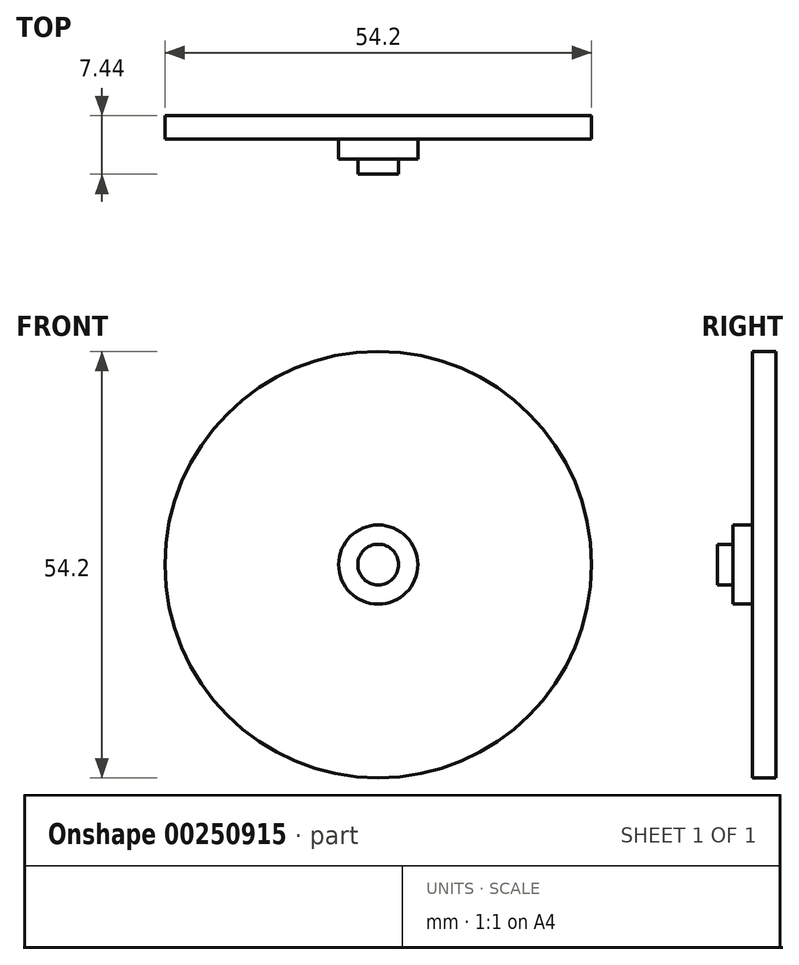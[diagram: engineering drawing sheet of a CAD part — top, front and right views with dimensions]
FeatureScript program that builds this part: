
annotation { "Feature Type Name" : "Feature", "Feature Type Description" : "" }
export const myFeature = defineFeature(function(context is Context, id is Id, definition is map)
    precondition{}
    {
        {
            var Q0;
            Q0=qCreatedBy(makeId("Front.planeOp"),FACE);
            var sketch = newSketch(context, id + "F0", { "sketchPlane" : qUnion([Q0])});
            skCircle(sketch, "E0", {"center": v(0, 0) * mm, "radius": 27.1 * mm});
            skSolve(sketch);
        }
        {
            var Q0;
            Q0=makeQuery(id+"F0.imprint","IMPRINT",FACE,{"disambiguationData":[TD([[makeQuery(id+"F0.imprint","IMPRINT",EDGE,{"derivedFrom":sQuery(id+"F0.wireOp",EDGE,"E0")}),1.0]])]});
            extrude(context, id + "F1", {"entities" : qUnion([Q0]), "endBound" : BoundingType.SYMMETRIC, "depth" : 3 * mm});
        }
        {
            var Q0;
            Q0=makeQuery(id+"F1.opExtrude","CAP_FACE",FACE,{"disambiguationData":[OSD([sQuery(id+"F0.wireOp",EDGE,"E0")])],"isStart":false});
            var sketch = newSketch(context, id + "F2", { "sketchPlane" : qUnion([Q0])});
            skCircle(sketch, "E1", {"center": v(0, 0) * mm, "radius": 5.03 * mm});
            skSolve(sketch);
        }
        {
            var Q0;
            Q0=makeQuery(id+"F2.imprint","IMPRINT",FACE,{"disambiguationData":[TD([[makeQuery(id+"F2.imprint","IMPRINT",EDGE,{"derivedFrom":sQuery(id+"F2.wireOp",EDGE,"E1")}),1.0]])]});
            extrude(context, id + "F3", {"entities" : qUnion([Q0]), "operationType" : NewBodyOperationType.ADD, "depth" : 2.5 * mm});
        }
        {
            var Q0;
            Q0=makeQuery(id+"F3.opExtrude","CAP_FACE",FACE,{"disambiguationData":[OSD([sQuery(id+"F2.wireOp",EDGE,"E1")])],"isStart":false});
            shell(context, id + "F4", {"entities" : qUnion([Q0]), "thickness" : 2.44 * mm});
        }
        {
            var Q0;
            Q0=makeQuery(id+"F4.opShell","OFFSET_FACE",FACE,{"disambiguationData":[OSD([sQuery(id+"F0.wireOp",EDGE,"E0")])]});
            extrude(context, id + "F5", {"entities" : qUnion([Q0]), "operationType" : NewBodyOperationType.ADD, "depth" : 5 * mm});
        }
    });
